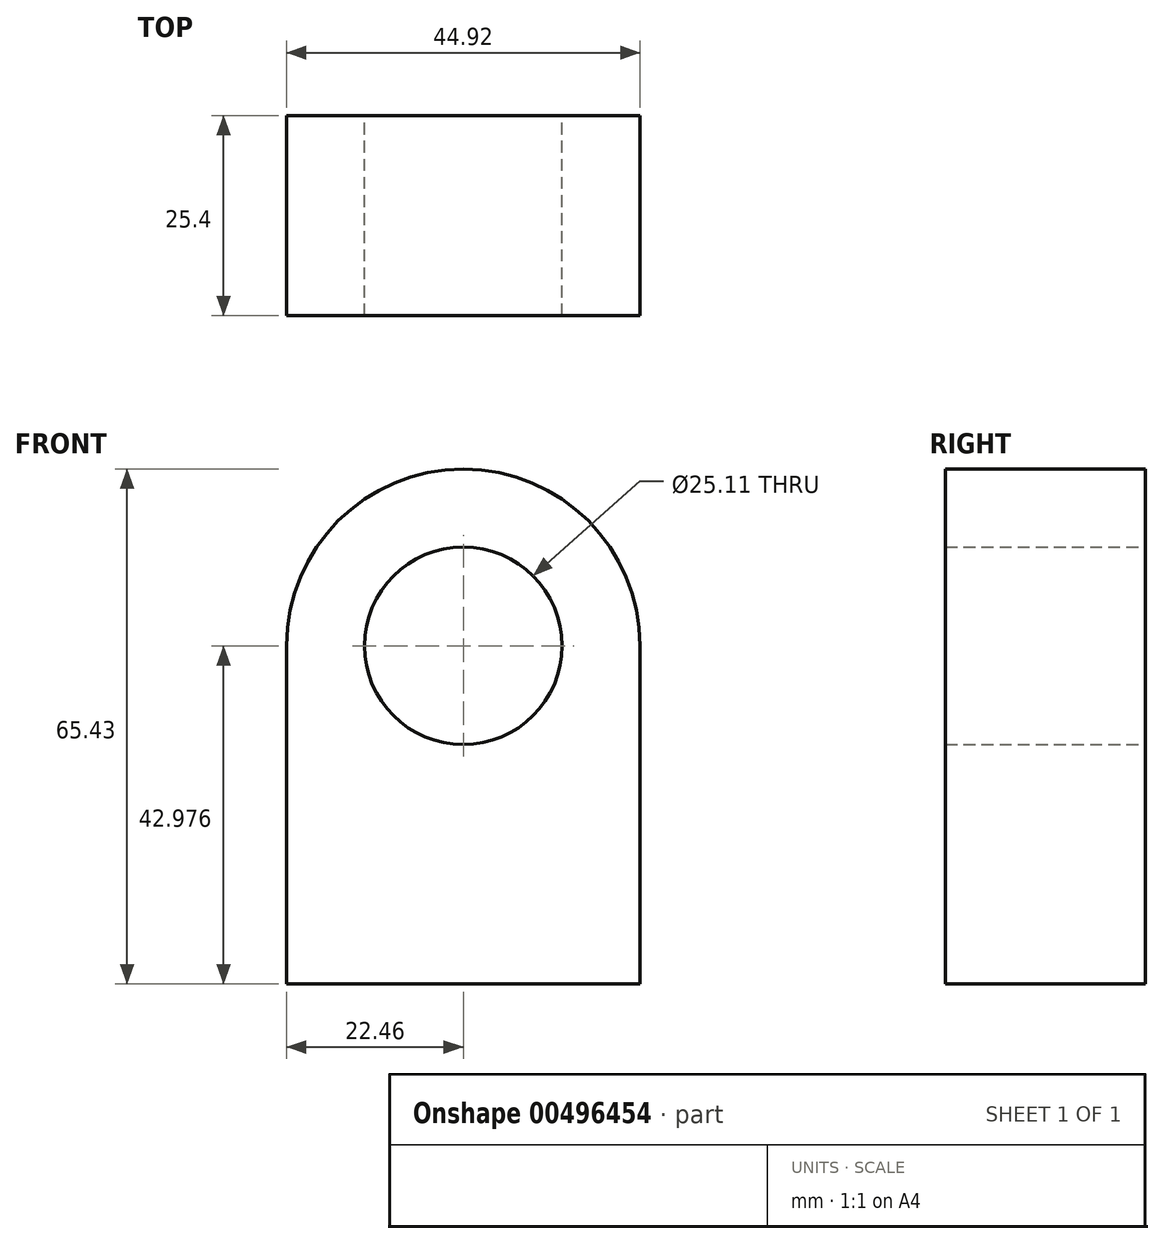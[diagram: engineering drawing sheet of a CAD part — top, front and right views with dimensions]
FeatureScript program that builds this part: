
annotation { "Feature Type Name" : "Feature", "Feature Type Description" : "" }
export const myFeature = defineFeature(function(context is Context, id is Id, definition is map)
    precondition{}
    {
        {
            var Q0;
            Q0=qCreatedBy(makeId("Front.planeOp"),FACE);
            var sketch = newSketch(context, id + "F0", { "sketchPlane" : qUnion([Q0])});
            skLineSegment(sketch, "E0.bottom", {"start": v(22.46, -21.49) * mm, "end": v(-22.46, -21.49) * mm});
            skLineSegment(sketch, "E0.left", {"start": v(22.46, -21.49) * mm, "end": v(22.46, 21.49) * mm});
            skLineSegment(sketch, "E0.right", {"start": v(-22.46, -21.49) * mm, "end": v(-22.46, 21.49) * mm});
            skPoint(sketch, "E0.middle", {"position": v(0, 0) * mm});
            skArc(sketch, "E1", {"start": v(22.46, 21.49) * mm, "mid": v(0, 43.94) * mm, "end": v(-22.46, 21.49) * mm});
            skCircle(sketch, "E2", {"center": v(0, 21.49) * mm, "radius": 12.56 * mm});
            skSolve(sketch);
        }
        {
            var Q0;
            Q0=makeQuery(id+"F0.imprint","IMPRINT",FACE,{"disambiguationData":[TD([[makeQuery(id+"F0.imprint","IMPRINT",EDGE,{"derivedFrom":sQuery(id+"F0.wireOp",EDGE,"E0.bottom")}),-1.0]])]});
            extrude(context, id + "F1", {"entities" : qUnion([Q0]), "depth" : 25.4 * mm});
        }
    });
